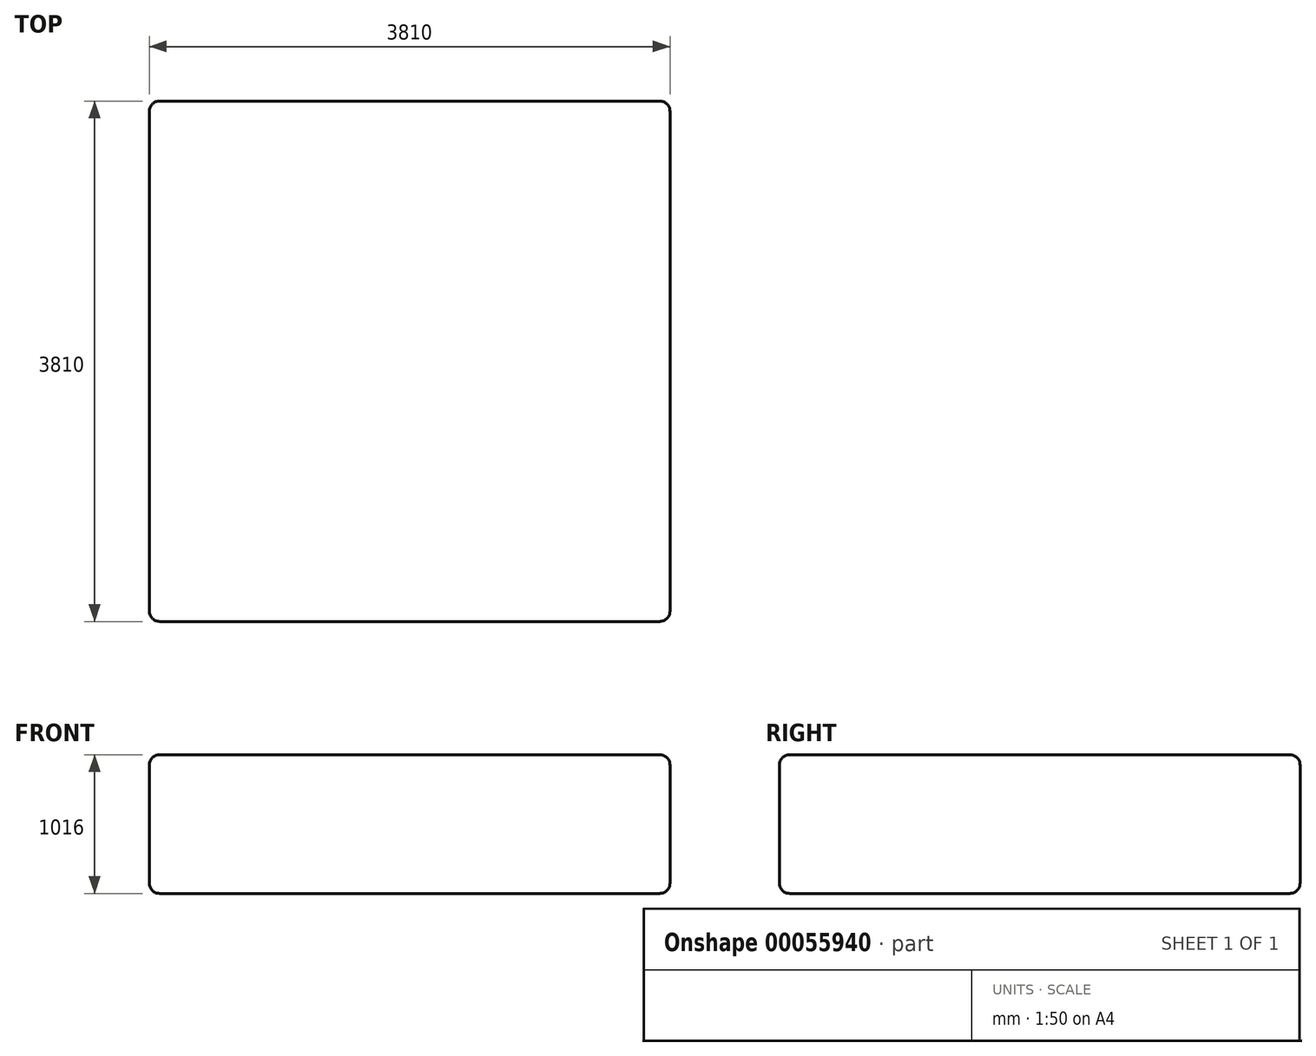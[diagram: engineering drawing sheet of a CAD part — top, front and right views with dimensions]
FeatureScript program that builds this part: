
annotation { "Feature Type Name" : "Feature", "Feature Type Description" : "" }
export const myFeature = defineFeature(function(context is Context, id is Id, definition is map)
    precondition{}
    {
        {
            var Q0;
            Q0=qCreatedBy(makeId("Front.planeOp"),FACE);
            var Q1;
            Q1=qCreatedBy(makeId("Front.planeOp"),FACE);
            var sketch = newSketch(context, id + "F0", { "sketchPlane" : qUnion([Q0, Q1])});
            skLineSegment(sketch, "E0", {"start": v(-1653.12, 527.5) * mm, "end": v(2156.88, 527.5) * mm});
            skLineSegment(sketch, "E1", {"start": v(-1653.12, 527.5) * mm, "end": v(-1653.12, -488.5) * mm});
            skLineSegment(sketch, "E2", {"start": v(2156.88, 527.5) * mm, "end": v(2156.88, -488.5) * mm});
            skLineSegment(sketch, "E3", {"start": v(-1653.12, -488.5) * mm, "end": v(2156.88, -488.5) * mm});
            skSolve(sketch);
        }
        {
            var Q0;
            Q0 = qSketchRegion(id + "F0", true);
            var Q1;
            Q1=makeQuery(id+"F0.imprint","IMPRINT",FACE,{"disambiguationData":[TD([[makeQuery(id+"F0.imprint","IMPRINT",EDGE,{"derivedFrom":sQuery(id+"F0.wireOp",EDGE,"E0")}),-1.0]])]});
            extrude(context, id + "F1", {"entities" : qUnion([Q0, Q1]), "depth" : 3810 * mm});
        }
        {
            var Q0;
            Q0=makeQuery(id+"F1.opExtrude","CAP_EDGE",EDGE,{"disambiguationData":[OSD([sQuery(id+"F0.wireOp",EDGE,"E0")])],"isStart":false});
            var Q1;
            Q1=makeQuery(id+"F1.opExtrude","SWEPT_EDGE",EDGE,{"disambiguationData":[OSD([sQuery(id+"F0.wireOp",EDGE,"E0"),sQuery(id+"F0.wireOp",EDGE,"E1")])]});
            var Q2;
            Q2=makeQuery(id+"F1.opExtrude","CAP_EDGE",EDGE,{"disambiguationData":[OSD([sQuery(id+"F0.wireOp",EDGE,"E0")])],"isStart":true});
            var Q3;
            Q3=makeQuery(id+"F1.opExtrude","SWEPT_EDGE",EDGE,{"disambiguationData":[OSD([sQuery(id+"F0.wireOp",EDGE,"E0"),sQuery(id+"F0.wireOp",EDGE,"E2")])]});
            var Q4;
            Q4=makeQuery(id+"F1.opExtrude","CAP_EDGE",EDGE,{"disambiguationData":[OSD([sQuery(id+"F0.wireOp",EDGE,"E2")])],"isStart":true});
            var Q5;
            Q5=makeQuery(id+"F1.opExtrude","CAP_EDGE",EDGE,{"disambiguationData":[OSD([sQuery(id+"F0.wireOp",EDGE,"E2")])],"isStart":false});
            var Q6;
            Q6=makeQuery(id+"F1.opExtrude","CAP_FACE",FACE,{"disambiguationData":[OSD([sQuery(id+"F0.wireOp",EDGE,"E0"),sQuery(id+"F0.wireOp",EDGE,"E1"),sQuery(id+"F0.wireOp",EDGE,"E2"),sQuery(id+"F0.wireOp",EDGE,"E3")])],"isStart":true});
            var Q7;
            Q7=makeQuery(id+"F1.opExtrude","CAP_EDGE",EDGE,{"disambiguationData":[OSD([sQuery(id+"F0.wireOp",EDGE,"E1")])],"isStart":false});
            var Q8;
            Q8=makeQuery(id+"F1.opExtrude","CAP_EDGE",EDGE,{"disambiguationData":[OSD([sQuery(id+"F0.wireOp",EDGE,"E3")])],"isStart":false});
            var Q9;
            Q9=makeQuery(id+"F1.opExtrude","SWEPT_EDGE",EDGE,{"disambiguationData":[OSD([sQuery(id+"F0.wireOp",EDGE,"E2"),sQuery(id+"F0.wireOp",EDGE,"E3")])]});
            var Q10;
            Q10=makeQuery(id+"F1.opExtrude","CAP_EDGE",EDGE,{"disambiguationData":[OSD([sQuery(id+"F0.wireOp",EDGE,"E3")])],"isStart":true});
            var Q11;
            Q11=makeQuery(id+"F1.opExtrude","SWEPT_EDGE",EDGE,{"disambiguationData":[OSD([sQuery(id+"F0.wireOp",EDGE,"E1"),sQuery(id+"F0.wireOp",EDGE,"E3")])]});
            fillet(context, id + "F2", {"entities" : qUnion([Q0, Q1, Q2, Q3, Q4, Q5, Q6, Q7, Q8, Q9, Q10, Q11]), "radius" : 76.2 * mm, "tangentPropagation" : true, "allowEdgeOverflow" : false});
        }
    });
